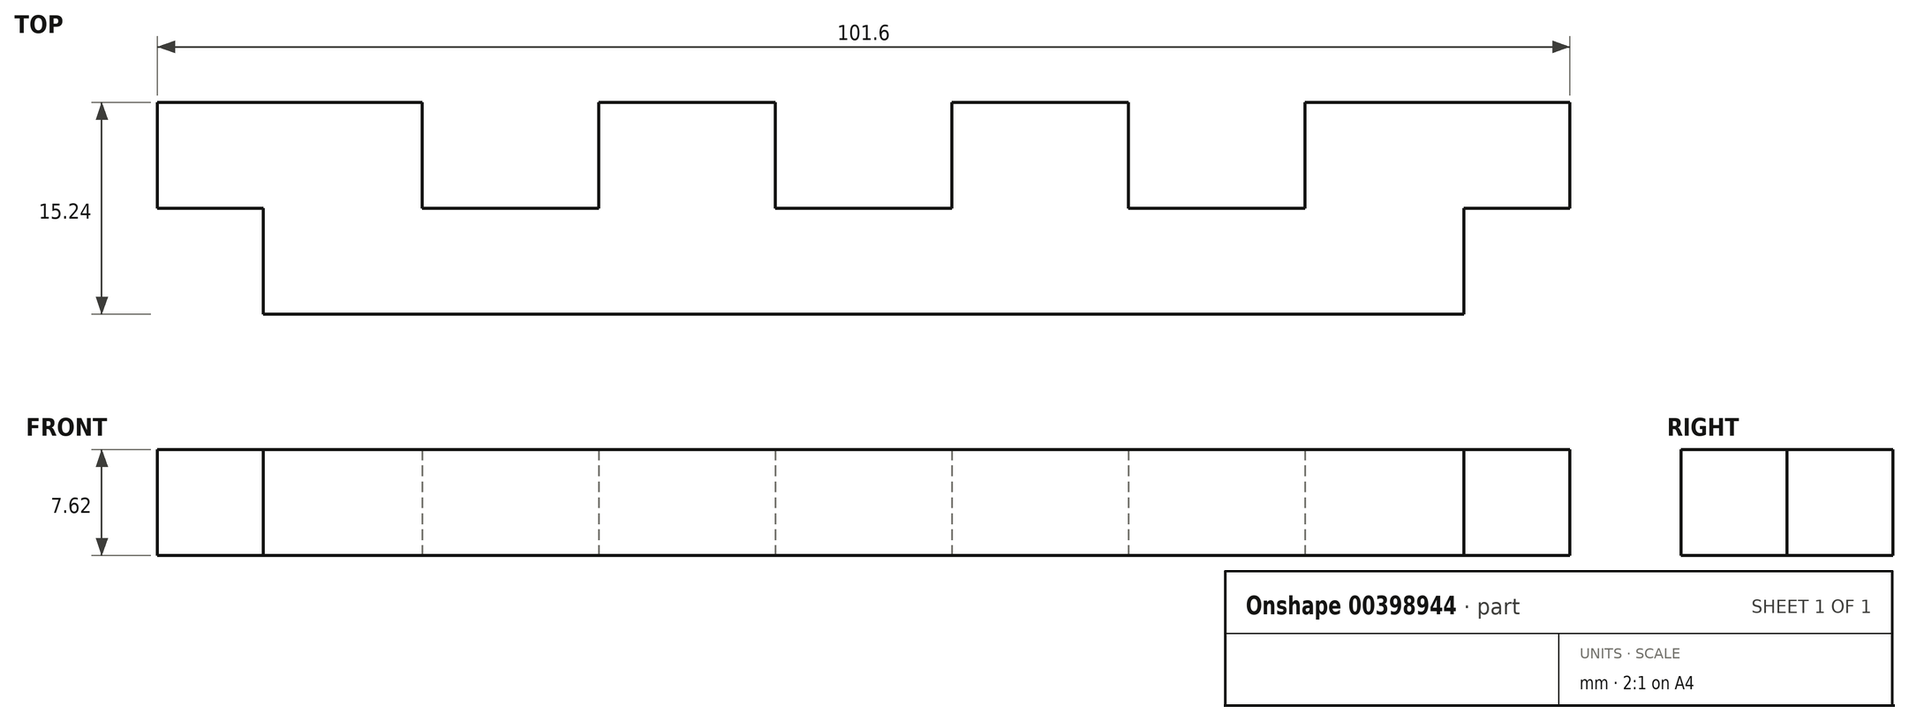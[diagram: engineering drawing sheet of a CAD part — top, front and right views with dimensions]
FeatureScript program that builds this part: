
annotation { "Feature Type Name" : "Feature", "Feature Type Description" : "" }
export const myFeature = defineFeature(function(context is Context, id is Id, definition is map)
    precondition{}
    {
        {
            var Q0;
            Q0=qCreatedBy(makeId("Top.planeOp"),FACE);
            var sketch = newSketch(context, id + "F0", { "sketchPlane" : qUnion([Q0])});
            skLineSegment(sketch, "E0.bottom", {"start": v(0, 0) * mm, "end": v(19.05, 0) * mm});
            skLineSegment(sketch, "E0.top", {"start": v(7.62, -15.24) * mm, "end": v(93.98, -15.24) * mm});
            skLineSegment(sketch, "E0.left", {"start": v(0, 0) * mm, "end": v(0, -7.62) * mm});
            skLineSegment(sketch, "E0.right", {"start": v(101.6, 0) * mm, "end": v(101.6, -7.62) * mm});
            skLineSegment(sketch, "E1", {"start": v(19.05, 0) * mm, "end": v(19.05, -7.62) * mm});
            skLineSegment(sketch, "E2", {"start": v(19.05, -7.62) * mm, "end": v(31.75, -7.62) * mm});
            skLineSegment(sketch, "E3", {"start": v(31.75, -7.62) * mm, "end": v(31.75, 0) * mm});
            skLineSegment(sketch, "E4", {"start": v(31.75, 0) * mm, "end": v(44.45, 0) * mm});
            skLineSegment(sketch, "E5", {"start": v(44.45, 0) * mm, "end": v(44.45, -7.62) * mm});
            skLineSegment(sketch, "E6", {"start": v(44.45, -7.62) * mm, "end": v(57.15, -7.62) * mm});
            skLineSegment(sketch, "E7", {"start": v(57.15, -7.62) * mm, "end": v(57.15, 0) * mm});
            skLineSegment(sketch, "E8", {"start": v(57.15, 0) * mm, "end": v(69.85, 0) * mm});
            skLineSegment(sketch, "E9", {"start": v(69.85, 0) * mm, "end": v(69.85, -7.62) * mm});
            skLineSegment(sketch, "E10", {"start": v(69.85, -7.62) * mm, "end": v(82.55, -7.62) * mm});
            skLineSegment(sketch, "E11", {"start": v(82.55, -7.62) * mm, "end": v(82.55, 0) * mm});
            skLineSegment(sketch, "E12.trimOffspring", {"start": v(82.55, 0) * mm, "end": v(101.6, 0) * mm});
            skLineSegment(sketch, "E13", {"start": v(0, -7.62) * mm, "end": v(7.62, -7.62) * mm});
            skLineSegment(sketch, "E14", {"start": v(7.62, -7.62) * mm, "end": v(7.62, -15.24) * mm});
            skPoint(sketch, "E15.orphan", {"position": v(0, -15.24) * mm});
            skLineSegment(sketch, "E16", {"start": v(101.6, -7.62) * mm, "end": v(93.98, -7.62) * mm});
            skLineSegment(sketch, "E17", {"start": v(93.98, -7.62) * mm, "end": v(93.98, -15.24) * mm});
            skSolve(sketch);
        }
        {
            var Q0;
            Q0=makeQuery(id+"F0.imprint","IMPRINT",FACE,{"disambiguationData":[TD([[makeQuery(id+"F0.imprint","IMPRINT",EDGE,{"derivedFrom":sQuery(id+"F0.wireOp",EDGE,"E0.top")}),1.0]])]});
            extrude(context, id + "F1", {"entities" : qUnion([Q0]), "depth" : 7.62 * mm, "offsetDistance" : 25.4 * mm});
        }
    });
